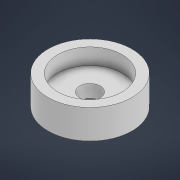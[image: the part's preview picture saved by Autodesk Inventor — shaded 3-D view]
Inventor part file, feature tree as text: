
AUTODESK INVENTOR PART (.ipt)
format: ipt  version: 2021 (Build 250183000, 183)  size: 109,568 bytes
history: native  units: mm
features: extrude x3, sketch x3
ambient origin geometry x8: Origin, YZ Plane, XZ Plane, XY Plane, X Axis, Y Axis, Z Axis, Center Point
bodies: Volumenkörper1 (feature_tree)
feature tree (6):
  extrude  "Extrusion1"  Depth=2.0mm TaperAngle=0.0deg
  extrude  "Extrusion2"  Depth=10.0mm
  extrude  "Extrusion3"  Depth=2.5mm
  sketch  "Skizze1"  dims[d0=13.0mm d1=2.0mm d2=0.0mm]
  sketch  "Skizze2"  dims[d3=10.0mm d4=13.0mm]
  sketch  "Skizze3"  dims[d5=2.5mm d6=0.0mm d7=3.2mm d8=2.5mm d9=0.0mm]
